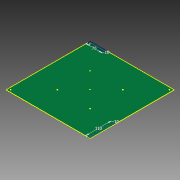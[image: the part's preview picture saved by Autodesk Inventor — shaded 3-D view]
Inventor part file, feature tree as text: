
AUTODESK INVENTOR PART (.ipt)
format: ipt  version: 2013 SP1 (Build 170176100, 176)  size: 115,712 bytes
history: native  units: mm
features: hole x2, pattern_linear x2, sketch x2, extrude x1
ambient origin geometry x8: Origin, YZ Plane, XZ Plane, XY Plane, X Axis, Y Axis, Z Axis, Center Point
bodies: Volumenkörper1 (feature_tree)
feature tree (7):
  extrude  "Extrusion1"  Depth=360.0mm
  hole  "Bohrung1"  [1 undecoded]
  pattern_linear  "Rechteckige Anordnung1"  Count1=2  [1 undecoded]
  hole  "Bohrung2"  [1 undecoded]
  pattern_linear  "Rechteckige Anordnung2"  Count1=11  [1 undecoded]
  sketch  "Skizze2"  dims[d2=2.0mm d3=0.0mm d4=10.0mm d5=10.0mm d6=3.0mm d7=6.0mm d8=4.0mm d9=2.0mm d10=90.0deg d11=8.0mm d12=20.594885mm d13=20.0mm d15=340.0mm d16=20.0mm d18=340.0mm d19=110.0mm d20=110.0mm d21=3.0mm d22=6.0mm d23=4.0mm d24=2.0mm d25=90.0deg d26=8.0mm d27=20.594885mm d28=20.0mm d30=140.0mm d31=20.0mm d33=140.0mm d34=70.0mm d35=10.0mm d38=10.0mm d39=110.0mm]
  sketch  "Skizze1"  dims[d0=360.0mm d1=360.0mm]
note: 4 required parameter values undecoded (feature->parameter linkage not recoverable at this tier; creation-order binding heuristic only, values carry confidence <= 0.55)
